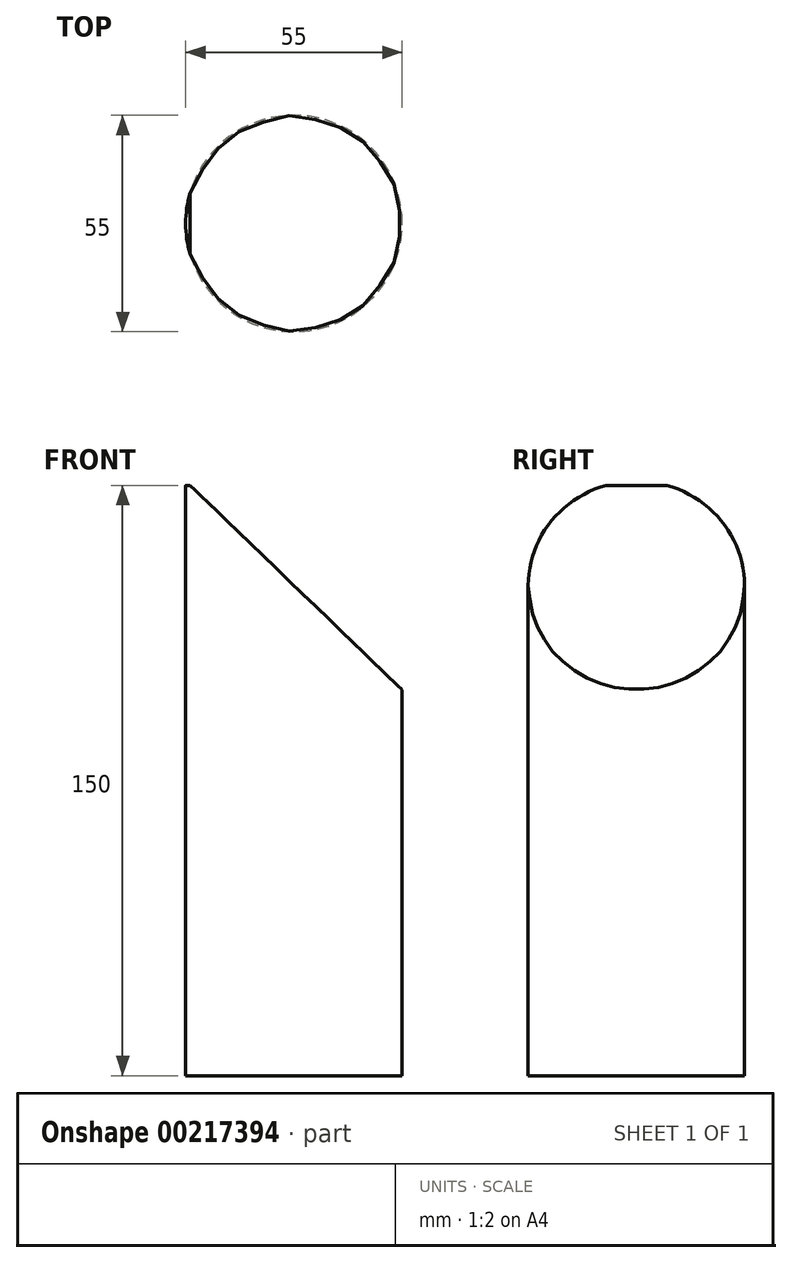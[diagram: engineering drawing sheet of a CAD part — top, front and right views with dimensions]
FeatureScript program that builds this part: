
annotation { "Feature Type Name" : "Feature", "Feature Type Description" : "" }
export const myFeature = defineFeature(function(context is Context, id is Id, definition is map)
    precondition{}
    {
        {
            var Q0;
            Q0=qCreatedBy(makeId("Top.planeOp"),FACE);
            var sketch = newSketch(context, id + "F0", { "sketchPlane" : qUnion([Q0])});
            skCircle(sketch, "E0", {"center": v(0, 0) * mm, "radius": 27.5 * mm});
            skSolve(sketch);
        }
        {
            var Q0;
            Q0=makeQuery(id+"F0.imprint","IMPRINT",FACE,{"disambiguationData":[TD([[makeQuery(id+"F0.imprint","IMPRINT",EDGE,{"derivedFrom":sQuery(id+"F0.wireOp",EDGE,"E0")}),1.0]])]});
            extrude(context, id + "F1", {"entities" : qUnion([Q0]), "depth" : 150 * mm});
        }
        {
            var Q0;
            Q0=qCreatedBy(makeId("Front.planeOp"),FACE);
            var sketch = newSketch(context, id + "F2", { "sketchPlane" : qUnion([Q0])});
            skLineSegment(sketch, "E1.bottom", {"start": v(-29.5, 153) * mm, "end": v(27.5, 153) * mm});
            skLineSegment(sketch, "E1.top", {"start": v(-29.5, 98) * mm, "end": v(27.5, 98) * mm});
            skLineSegment(sketch, "E1.left", {"start": v(-29.5, 153) * mm, "end": v(-29.5, 98) * mm});
            skLineSegment(sketch, "E1.right", {"start": v(27.5, 153) * mm, "end": v(27.5, 98) * mm});
            skLineSegment(sketch, "E2", {"start": v(-29.5, 153) * mm, "end": v(27.5, 98) * mm});
            skSolve(sketch);
        }
        {
            var Q0;
            Q0=makeQuery(id+"F2.imprint","IMPRINT",FACE,{"disambiguationData":[TD([[makeQuery(id+"F2.imprint","IMPRINT",EDGE,{"derivedFrom":sQuery(id+"F2.wireOp",EDGE,"E1.bottom")}),-1.0]])]});
            extrude(context, id + "F3", {"entities" : qUnion([Q0]), "depth" : 27.5 * mm, "hasSecondDirection" : true, "secondDirectionOppositeDirection" : true, "secondDirectionDepth" : 27.5 * mm});
        }
        {
            var Q0;
            Q0=makeQuery(id+"F3.opExtrude","SWEPT_BODY",BODY,{"disambiguationData":[OSD([sQuery(id+"F2.wireOp",EDGE,"E1.bottom"),sQuery(id+"F2.wireOp",EDGE,"E1.right"),sQuery(id+"F2.wireOp",EDGE,"E2")])]});
            var Q1;
            Q1=makeQuery(id+"F1.opExtrude","SWEPT_BODY",BODY,{"disambiguationData":[OSD([sQuery(id+"F0.wireOp",EDGE,"E0")])]});
            booleanBodies(context, id + "F4", {"operationType" : BooleanOperationType.SUBTRACTION, "tools" : qUnion([Q0]), "targets" : qUnion([Q1])});
        }
    });
